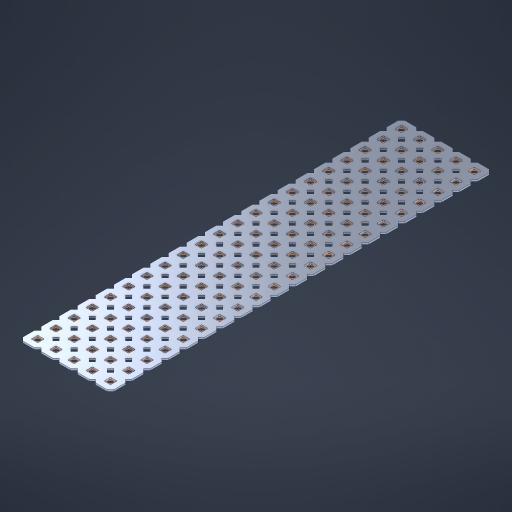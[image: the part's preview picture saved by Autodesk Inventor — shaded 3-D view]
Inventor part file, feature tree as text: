
AUTODESK INVENTOR PART (.ipt)
format: ipt  version: 2023 (Build 270158000, 158)  size: 1,475,584 bytes
history: native  units: in
note: dims shown in document units (in); Inventor stores cm internally (conversion verified against a paired STEP export)
features: other x106, extrude x104, sketch x2, pattern_linear x1
ambient origin geometry x8: Origin, YZ Plane, XZ Plane, XY Plane, X Axis, Y Axis, Z Axis, Center Point
bodies: Solid1 (feature_tree), Body (feature_tree)
feature tree (213):
  pattern_linear  "Rectangular Pattern1"  Spacing1=0.09in  [1 undecoded]
  sketch  "Sketch1"  dims[d1=0.5in]
  sketch  "Sketch2"  dims[d2=0.182in d3=0.09in d4=0.09in d5=0.09in d6=0.09in d7=0.09in d8=0.09in d9=0.09in d10=0.09in d11=0.02in d13=0.0in d14=0.172in d15=0.0625in d16=0.0in d19=0.5in d22=0.5in]
  other  "Srf1"
  other  "Srf126"
  other  "Srf127"
  other  "Srf128"
  other  "Srf129"
  other  "Srf130"
  other  "Srf131"
  other  "Srf250"
  other  "Srf251"
  other  "Srf252"
  other  "Srf253"
  other  "Srf254"
  other  "Srf255"
  other  "Srf256"
  other  "Srf257"
  other  "Srf258"
  other  "Srf259"
  other  "Srf260"
  other  "Srf261"
  other  "Srf262"
  other  "Srf263"
  other  "Srf268"
  other  "Srf269"
  other  "Srf270"
  other  "Srf271"
  other  "Srf272"
  other  "Srf273"
  other  "Srf274"
  other  "Srf275"
  other  "Srf276"
  other  "Srf277"
  other  "Srf278"
  other  "Srf279"
  other  "Srf280"
  other  "Srf281"
  other  "Srf282"
  other  "Srf283"
  other  "Srf284"
  other  "Srf285"
  other  "Srf286"
  other  "Srf287"
  other  "Srf288"
  other  "Srf293"
  other  "Srf294"
  other  "Srf295"
  other  "Srf296"
  other  "Srf297"
  other  "Srf298"
  other  "Srf299"
  other  "Srf300"
  other  "Srf301"
  other  "Srf302"
  other  "Srf303"
  other  "Srf304"
  other  "Srf305"
  other  "Srf306"
  other  "Srf307"
  other  "Srf308"
  other  "Srf309"
  other  "Srf310"
  other  "Srf311"
  other  "Srf312"
  other  "Srf313"
  other  "Srf318"
  other  "Srf319"
  other  "Srf320"
  other  "Srf321"
  other  "Srf322"
  other  "Srf323"
  other  "Srf324"
  other  "Srf325"
  other  "Srf326"
  other  "Srf327"
  other  "Srf328"
  other  "Srf329"
  other  "Srf330"
  other  "Srf331"
  other  "Srf332"
  other  "Srf333"
  other  "Srf334"
  other  "Srf335"
  other  "Srf336"
  other  "Srf337"
  other  "Srf338"
  other  "Srf343"
  other  "Srf344"
  other  "Srf345"
  other  "Srf346"
  other  "Srf347"
  other  "Srf348"
  other  "Srf349"
  other  "Srf350"
  other  "Srf351"
  other  "Srf352"
  other  "Srf353"
  other  "Srf354"
  other  "Srf355"
  other  "Srf356"
  other  "Srf357"
  other  "Srf358"
  other  "Srf359"
  other  "Srf360"
  other  "Srf361"
  other  "Srf362"
  other  "Srf363"
  other  "Circle"
  extrude  "ExtrusionSrf126"  Depth=0.09in
  extrude  "ExtrusionSrf127"  Depth=0.09in
  extrude  "ExtrusionSrf128"  Depth=0.09in
  extrude  "ExtrusionSrf129"  Depth=0.09in
  extrude  "ExtrusionSrf130"  Depth=0.09in
  extrude  "ExtrusionSrf131"  Depth=0.09in
  extrude  "ExtrusionSrf250"  Depth=0.09in
  extrude  "ExtrusionSrf251"  Depth=0.02in
  extrude  "ExtrusionSrf252"  TaperAngle=0.0deg  [1 undecoded]
  extrude  "ExtrusionSrf253"  Depth=0.5in
  extrude  "ExtrusionSrf254"  Depth=0.5in TaperAngle=0.0deg
  extrude  "ExtrusionSrf255"  Depth=0.5in
  extrude  "ExtrusionSrf256"  Depth=0.5in
  extrude  "ExtrusionSrf257"  [1 undecoded]
  extrude  "ExtrusionSrf258"  [1 undecoded]
  extrude  "ExtrusionSrf259"  [1 undecoded]
  extrude  "ExtrusionSrf260"  [1 undecoded]
  extrude  "ExtrusionSrf261"  [1 undecoded]
  extrude  "ExtrusionSrf262"  [1 undecoded]
  extrude  "ExtrusionSrf263"  [1 undecoded]
  extrude  "ExtrusionSrf268"  [1 undecoded]
  extrude  "ExtrusionSrf269"  [1 undecoded]
  extrude  "ExtrusionSrf270"  [1 undecoded]
  extrude  "ExtrusionSrf271"  [1 undecoded]
  extrude  "ExtrusionSrf272"  [1 undecoded]
  extrude  "ExtrusionSrf273"  [1 undecoded]
  extrude  "ExtrusionSrf274"  [1 undecoded]
  extrude  "ExtrusionSrf275"  [1 undecoded]
  extrude  "ExtrusionSrf276"  [1 undecoded]
  extrude  "ExtrusionSrf277"  [1 undecoded]
  extrude  "ExtrusionSrf278"  [1 undecoded]
  extrude  "ExtrusionSrf279"  [1 undecoded]
  extrude  "ExtrusionSrf280"  [1 undecoded]
  extrude  "ExtrusionSrf281"  [1 undecoded]
  extrude  "ExtrusionSrf282"  [1 undecoded]
  extrude  "ExtrusionSrf283"  [1 undecoded]
  extrude  "ExtrusionSrf284"  [1 undecoded]
  extrude  "ExtrusionSrf285"  [1 undecoded]
  extrude  "ExtrusionSrf286"  [1 undecoded]
  extrude  "ExtrusionSrf287"  [1 undecoded]
  extrude  "ExtrusionSrf288"  [1 undecoded]
  extrude  "ExtrusionSrf293"  [1 undecoded]
  extrude  "ExtrusionSrf294"  [1 undecoded]
  extrude  "ExtrusionSrf295"  [1 undecoded]
  extrude  "ExtrusionSrf296"  [1 undecoded]
  extrude  "ExtrusionSrf297"  [1 undecoded]
  extrude  "ExtrusionSrf298"  [1 undecoded]
  extrude  "ExtrusionSrf299"  [1 undecoded]
  extrude  "ExtrusionSrf300"  [1 undecoded]
  extrude  "ExtrusionSrf301"  [1 undecoded]
  extrude  "ExtrusionSrf302"  [1 undecoded]
  extrude  "ExtrusionSrf303"  [1 undecoded]
  extrude  "ExtrusionSrf304"  [1 undecoded]
  extrude  "ExtrusionSrf305"  [1 undecoded]
  extrude  "ExtrusionSrf306"  [1 undecoded]
  extrude  "ExtrusionSrf307"  [1 undecoded]
  extrude  "ExtrusionSrf308"  [1 undecoded]
  extrude  "ExtrusionSrf309"  [1 undecoded]
  extrude  "ExtrusionSrf310"  [1 undecoded]
  extrude  "ExtrusionSrf311"  [1 undecoded]
  extrude  "ExtrusionSrf312"  [1 undecoded]
  extrude  "ExtrusionSrf313"  [1 undecoded]
  extrude  "ExtrusionSrf318"  [1 undecoded]
  extrude  "ExtrusionSrf319"  [1 undecoded]
  extrude  "ExtrusionSrf320"  [1 undecoded]
  extrude  "ExtrusionSrf321"  [1 undecoded]
  extrude  "ExtrusionSrf322"  [1 undecoded]
  extrude  "ExtrusionSrf323"  [1 undecoded]
  extrude  "ExtrusionSrf324"  [1 undecoded]
  extrude  "ExtrusionSrf325"  [1 undecoded]
  extrude  "ExtrusionSrf326"  [1 undecoded]
  extrude  "ExtrusionSrf327"  [1 undecoded]
  extrude  "ExtrusionSrf328"  [1 undecoded]
  extrude  "ExtrusionSrf329"  [1 undecoded]
  extrude  "ExtrusionSrf330"  [1 undecoded]
  extrude  "ExtrusionSrf331"  [1 undecoded]
  extrude  "ExtrusionSrf332"  [1 undecoded]
  extrude  "ExtrusionSrf333"  [1 undecoded]
  extrude  "ExtrusionSrf334"  [1 undecoded]
  extrude  "ExtrusionSrf335"  [1 undecoded]
  extrude  "ExtrusionSrf336"  [1 undecoded]
  extrude  "ExtrusionSrf337"  [1 undecoded]
  extrude  "ExtrusionSrf338"  [1 undecoded]
  extrude  "ExtrusionSrf343"  [1 undecoded]
  extrude  "ExtrusionSrf344"  [1 undecoded]
  extrude  "ExtrusionSrf345"  [1 undecoded]
  extrude  "ExtrusionSrf346"  [1 undecoded]
  extrude  "ExtrusionSrf347"  [1 undecoded]
  extrude  "ExtrusionSrf348"  [1 undecoded]
  extrude  "ExtrusionSrf349"  [1 undecoded]
  extrude  "ExtrusionSrf350"  [1 undecoded]
  extrude  "ExtrusionSrf351"  [1 undecoded]
  extrude  "ExtrusionSrf352"  [1 undecoded]
  extrude  "ExtrusionSrf353"  [1 undecoded]
  extrude  "ExtrusionSrf354"  [1 undecoded]
  extrude  "ExtrusionSrf355"  [1 undecoded]
  extrude  "ExtrusionSrf356"  [1 undecoded]
  extrude  "ExtrusionSrf357"  [1 undecoded]
  extrude  "ExtrusionSrf358"  [1 undecoded]
  extrude  "ExtrusionSrf359"  [1 undecoded]
  extrude  "ExtrusionSrf360"  [1 undecoded]
  extrude  "ExtrusionSrf361"  [1 undecoded]
  extrude  "ExtrusionSrf362"  [1 undecoded]
  extrude  "ExtrusionSrf363"  [1 undecoded]
note: 93 required parameter values undecoded (feature->parameter linkage not recoverable at this tier; creation-order binding heuristic only, values carry confidence <= 0.55)
